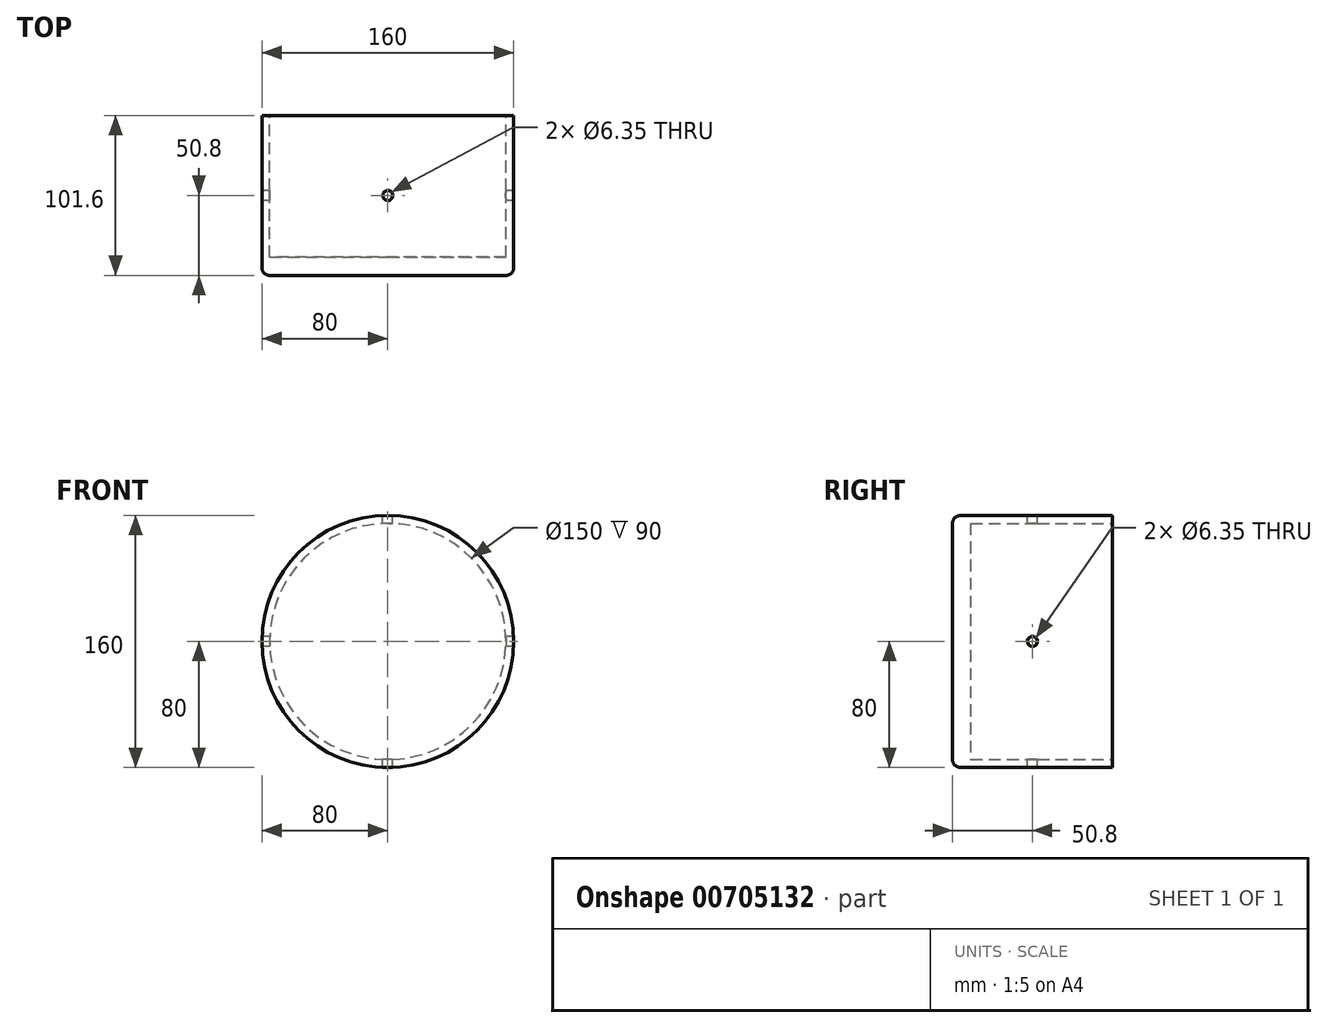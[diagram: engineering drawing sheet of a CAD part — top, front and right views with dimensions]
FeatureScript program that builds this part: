
annotation { "Feature Type Name" : "Feature", "Feature Type Description" : "" }
export const myFeature = defineFeature(function(context is Context, id is Id, definition is map)
    precondition{}
    {
        {
            var Q0;
            Q0=qCreatedBy(makeId("Front.planeOp"),FACE);
            var sketch = newSketch(context, id + "F0", { "sketchPlane" : qUnion([Q0])});
            skCircle(sketch, "E0", {"center": v(0, 0) * mm, "radius": 80 * mm});
            skSolve(sketch);
        }
        {
            var Q0;
            Q0 = qSketchRegion(id + "F0", true);
            extrude(context, id + "F1", {"entities" : qUnion([Q0]), "oppositeDirection" : true, "depth" : 101.6 * mm, "offsetDistance" : 25.4 * mm});
        }
        {
            var Q0;
            Q0=makeQuery(id+"F1.opExtrude","CAP_EDGE",EDGE,{"disambiguationData":[OSD([sQuery(id+"F0.wireOp",EDGE,"E0")])],"isStart":true});
            fillet(context, id + "F2", {"entities" : qUnion([Q0]), "radius" : 5.08 * mm, "tangentPropagation" : true, "allowEdgeOverflow" : false});
        }
        {
            var Q0;
            Q0=makeQuery(id+"F1.opExtrude","CAP_FACE",FACE,{"disambiguationData":[OSD([sQuery(id+"F0.wireOp",EDGE,"E0")])],"isStart":false});
            var sketch = newSketch(context, id + "F3", { "sketchPlane" : qUnion([Q0])});
            skCircle(sketch, "E1", {"center": v(0, 0) * mm, "radius": 75 * mm});
            skSolve(sketch);
        }
        {
            var Q0;
            Q0 = qSketchRegion(id + "F3", true);
            extrude(context, id + "F4", {"entities" : qUnion([Q0]), "operationType" : NewBodyOperationType.REMOVE, "oppositeDirection" : true, "depth" : 90 * mm, "offsetDistance" : 25 * mm});
        }
        {
            var Q0;
            Q0=qCreatedBy(makeId("Top.planeOp"),FACE);
            var sketch = newSketch(context, id + "F5", { "sketchPlane" : qUnion([Q0])});
            skCircle(sketch, "E2", {"center": v(0, 50.8) * mm, "radius": 3.18 * mm});
            skSolve(sketch);
        }
        {
            var Q0;
            Q0 = qSketchRegion(id + "F5", true);
            extrude(context, id + "F6", {"entities" : qUnion([Q0]), "operationType" : NewBodyOperationType.REMOVE, "endBound" : BoundingType.SYMMETRIC, "oppositeDirection" : true, "depth" : 254 * mm, "offsetDistance" : 25.4 * mm});
        }
        {
            var Q0;
            Q0=qCreatedBy(makeId("Right.planeOp"),FACE);
            var sketch = newSketch(context, id + "F7", { "sketchPlane" : qUnion([Q0])});
            skCircle(sketch, "E3", {"center": v(50.8, 0) * mm, "radius": 3.17 * mm});
            skSolve(sketch);
        }
        {
            var Q0;
            Q0 = qSketchRegion(id + "F7", true);
            extrude(context, id + "F8", {"entities" : qUnion([Q0]), "operationType" : NewBodyOperationType.REMOVE, "endBound" : BoundingType.SYMMETRIC, "depth" : 254 * mm, "offsetDistance" : 25.4 * mm});
        }
    });
